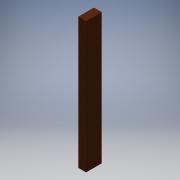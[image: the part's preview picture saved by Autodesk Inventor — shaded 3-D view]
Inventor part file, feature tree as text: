
AUTODESK INVENTOR PART (.ipt)
format: ipt  version: 2016 (Build 200138000, 138)  size: 95,232 bytes
history: native  units: in
note: dims shown in document units (in); Inventor stores cm internally (conversion verified against a paired STEP export)
features: extrude x1, sketch x1
ambient origin geometry x8: Origin, YZ Plane, XZ Plane, XY Plane, X Axis, Y Axis, Z Axis, Center Point
bodies: Solid1 (feature_tree)
feature tree (2):
  extrude  "Extrusion1"  Depth=1.5in
  sketch  "Sketch1"  dims[d0=0.75in d1=1.5in d2=12.5in d3=0.0in]
